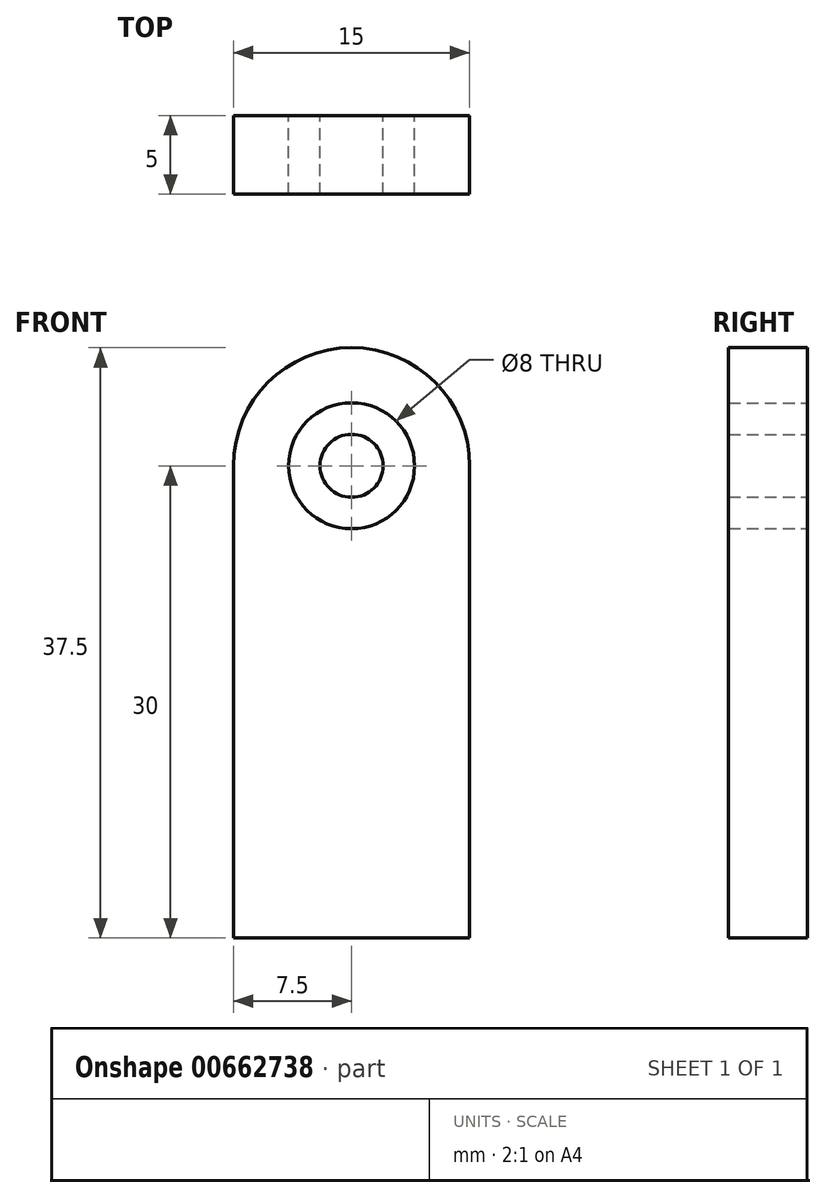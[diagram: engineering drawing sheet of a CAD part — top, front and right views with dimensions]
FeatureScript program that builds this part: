
annotation { "Feature Type Name" : "Feature", "Feature Type Description" : "" }
export const myFeature = defineFeature(function(context is Context, id is Id, definition is map)
    precondition{}
    {
        {
            var Q0;
            Q0=qCreatedBy(makeId("Front.planeOp"),FACE);
            var sketch = newSketch(context, id + "F0", { "sketchPlane" : qUnion([Q0])});
            skLineSegment(sketch, "E0.bottom", {"start": v(0, 0) * mm, "end": v(15, 0) * mm});
            skLineSegment(sketch, "E0.left", {"start": v(0, 0) * mm, "end": v(0, 30) * mm});
            skLineSegment(sketch, "E0.right", {"start": v(15, 0) * mm, "end": v(15, 30) * mm});
            skArc(sketch, "E1", {"start": v(15, 30) * mm, "mid": v(7.5, 37.5) * mm, "end": v(0, 30) * mm});
            skCircle(sketch, "E2", {"center": v(7.5, 30) * mm, "radius": 4 * mm});
            skCircle(sketch, "E3", {"center": v(7.5, 30) * mm, "radius": 2 * mm});
            skSolve(sketch);
        }
        {
            var Q0;
            Q0 = qSketchRegion(id + "F0", true);
            var Q1;
            Q1=makeQuery(id+"F0.imprint","IMPRINT",FACE,{"disambiguationData":[TD([[makeQuery(id+"F0.imprint","IMPRINT",EDGE,{"derivedFrom":sQuery(id+"F0.wireOp",EDGE,"E3")}),1.0]])]});
            extrude(context, id + "F1", {"entities" : qUnion([Q0, Q1]), "depth" : 5 * mm, "offsetDistance" : 25 * mm});
        }
    });
